MODEL slx_299e4cb9b980
CONFIG AbsTol = auto
CONFIG EnableMultiTasking = off
CONFIG FixedStep = 0.00001
CONFIG InitFcn = We_Speed = 900;
Unobservable = 0.7; % (0-0.866)
zeta = 0.05;
CONFIG MaxStep = auto
CONFIG MinStep = auto
CONFIG RelTol = 1e-3
CONFIG SampleTimeConstraint = Unconstrained
CONFIG SolverName = FixedStepAuto
CONFIG StartTime = 0.0
CONFIG StopTime = 2
BLOCK [TransferFcn]      BPF带通滤波    
  Denominator = [1 (zeta*We_Speed) (We_Speed)^2]
  Numerator = [(zeta*We_Speed) 0]
BLOCK [TransferFcn]   BPF带通滤波   
  Denominator = [1 (zeta*We_Speed) (We_Speed)^2]
  Numerator = [(zeta*We_Speed) 0]
BLOCK [TransferFcn] BPF带通滤波 
  Denominator = [1 (zeta*We_Speed) (We_Speed)^2]
  Numerator = [(zeta*We_Speed) 0]
BLOCK [Clock] Clock1
BLOCK [Constant] Constant13
  Value = We_Speed
BLOCK [Constant] Constant14
  Value = Unobservable
BLOCK [Delay] Delay5
  DelayLength = 1
  InputPortMap = u0
  InputProcessing = Columns as channels (frame based)
  NameLocation = top
BLOCK [Display] Display2
  Decimation = 1
BLOCK [SubSystem] MATLAB Function5
  ErrorFcn = Stateflow.Translate.translate
  PermitHierarchicalResolution = ExplicitOnly
  SFBlockType = MATLAB Function
  TreatAsAtomicUnit = on
BLOCK [Demux] MATLAB Function5/ Demux 
  Outputs = 1
BLOCK [S-Function] MATLAB Function5/ SFunction 
  EnableBusSupport = off
  FunctionName = sf_sfun
  PortCounts = [2 2]
  SFcnIsStateOwnerBlock = off
  SFunctionDeploymentMode = off
  Tag = Stateflow S-Function 6
BLOCK [Terminator] MATLAB Function5/ Terminator 
BLOCK [Inport] MATLAB Function5/max_prev
  Port = 2
BLOCK [Inport] MATLAB Function5/u
BLOCK [Outport] MATLAB Function5/y
  VectorParamsAs1DForOutWhenUnconnected = off
BLOCK [Scope] Scope4
  ActiveDisplayYMaximum = 1.2499999999852798
  ActiveDisplayYMinimum = -1.2499999999775429
  DataLoggingVariableName = ScopeData22
  Floating = off
  GraphicalSettings = {"AxesScalingProperties":{"AlignXAxis":"Center","AlignYAxis":"Center","AutoScaleXAxisLimits":false,"AxesScaling":"Manual","AxesScalingNumUpdates":10,"ExpandOnly":true,"ScaleAxesLimitsAtStop":false,"XAxisDataRange":100,"YAxisDataRange":80},"DisplayProperties":{"ColorOrder":["auto","auto","auto","auto","auto","auto","auto","auto","auto","auto","auto","auto","auto","auto","auto","auto","auto","auto",...<+2600ch>
  MultipleDisplayCache = [{"MaxYLimMag":1.2499999999852798,"MaxYLimReal":1.2499999999852798,"MinYLimMag":0,"MinYLimReal":-1.2499999999775429,"PlotAsMagnitudePhase":false,"ShowGrid":true,"ShowLegend":true,"Title":"%<SignalLabel>","YLabel":""}]
  NumInputPorts = 6
  ScopeFrameLocation = window
  ShowLegend = on
  WasSavedAsWebScope = on
  WindowPosition = [803.000000,170.000000,777.000000,541.000000,]
BLOCK [SubSystem] 原始采样数据
  ErrorFcn = Stateflow.Translate.translate
  PermitHierarchicalResolution = ExplicitOnly
  SFBlockType = MATLAB Function
  TreatAsAtomicUnit = on
BLOCK [Demux] 原始采样数据/ Demux 
  Outputs = 1
BLOCK [S-Function] 原始采样数据/ SFunction 
  EnableBusSupport = off
  FunctionName = sf_sfun
  PortCounts = [3 4]
  SFcnIsStateOwnerBlock = off
  SFunctionDeploymentMode = off
  Tag = Stateflow S-Function 5
BLOCK [Terminator] 原始采样数据/ Terminator 
BLOCK [Inport] 原始采样数据/ih
  Port = 2
BLOCK [Inport] 原始采样数据/t
  Port = 3
BLOCK [Inport] 原始采样数据/we
BLOCK [Outport] 原始采样数据/y_a
  VectorParamsAs1DForOutWhenUnconnected = off
BLOCK [Outport] 原始采样数据/y_b
  Port = 2
BLOCK [Outport] 原始采样数据/y_c
  Port = 3
BLOCK [Gain] 滤波处理后数据A
  Gain = 0.3436+0.4682*Unobservable+0.5278/((sqrt(3)/2)-Unobservable)
BLOCK [Gain] 滤波处理后数据B
  Gain = 0.3436+0.4682*Unobservable+0.5278/((sqrt(3)/2)-Unobservable)
BLOCK [Gain] 滤波处理后数据C
  Gain = 0.3436+0.4682*Unobservable+0.5278/((sqrt(3)/2)-Unobservable)
LINE      BPF带通滤波    :1 -> 滤波处理后数据C:1
LINE   BPF带通滤波   :1 -> 滤波处理后数据B:1
LINE BPF带通滤波 :1 -> MATLAB Function5:1
LINE BPF带通滤波 :1 -> 滤波处理后数据A:1
LINE Clock1:1 -> 原始采样数据:3
LINE Constant13:1 -> 原始采样数据:1
LINE Constant14:1 -> 原始采样数据:2
LINE Delay5:1 -> MATLAB Function5:2
LINE MATLAB Function5:1 -> Delay5:1
LINE MATLAB Function5:1 -> Display2:1
LINE 原始采样数据:1 -> BPF带通滤波 :1
LINE 原始采样数据:1 -> Scope4:1
LINE 原始采样数据:2 ->   BPF带通滤波   :1
LINE 原始采样数据:2 -> Scope4:3
LINE 原始采样数据:3 ->      BPF带通滤波    :1
LINE 原始采样数据:3 -> Scope4:5
LINE 滤波处理后数据A:1 -> Scope4:2
LINE 滤波处理后数据B:1 -> Scope4:4
LINE 滤波处理后数据C:1 -> Scope4:6
CHART 原始采样数据 states=1 transitions=1
  STATE_LABEL 'eML_blk_kernel()'
  STATE_LABEL 'SCRIPT:\nfunction [y_a, y_b, y_c] = fcn(we, ih, t)\n%#codegen\n% 输入：\n%   we - 角频率 (rad/s)\n%   ih - 不可观测区参数 (0 ~ sqrt(3)/2)，决定归零区间宽度\n%   t  - 仿真时间 (s)，从 Clock 模块输入\n% 输出：\n%   y_a, y_b, y_c - 修正后的三相正弦波（各相隔120°，每个波形在60°整数倍点左侧归零）\n\n% -------- 参数限幅 --------\nih_max = sqrt(3)/2;\nih_limited = min(abs(ih), ih_max);\n\n% -------- 归零宽度：asin(ih) 弧度，转为角度 --------\nzero_width_deg = asin(ih_limited) * 180 / pi;  % 0° ~ ...<+731ch>'
CHART MATLAB Function5 states=1 transitions=1
  STATE_LABEL 'eML_blk_kernel()'
  STATE_LABEL 'SCRIPT:\nfunction y = fcn(u, max_prev)\n%#codegen\n% 输入：\n%   u        - 当前输入数值\n%   max_prev - 上一拍的历史最大值（来自 Unit Delay）\n% 输出：\n%   y        - 新的历史最大值\n\n% 比较当前值和上一拍最大值\nif u > max_prev\n    y = u;\nelse\n    y = max_prev;\nend\n\nend'
CHART  states=0 transitions=0
CHART  states=0 transitions=0
